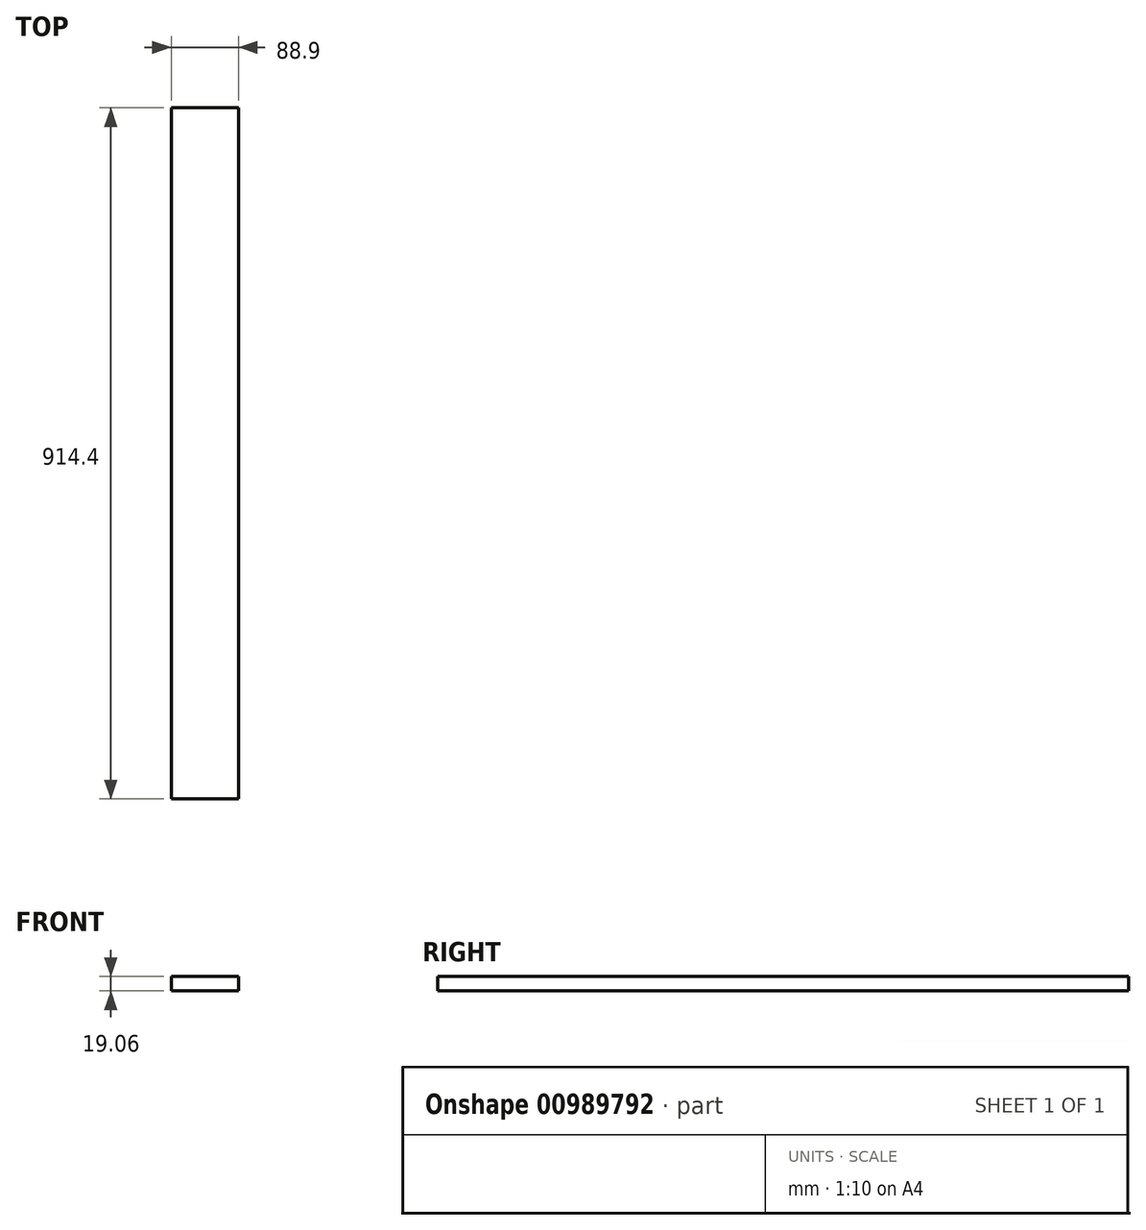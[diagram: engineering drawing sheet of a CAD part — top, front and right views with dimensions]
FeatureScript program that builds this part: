
annotation { "Feature Type Name" : "Feature", "Feature Type Description" : "" }
export const myFeature = defineFeature(function(context is Context, id is Id, definition is map)
    precondition{}
    {
        {
            var Q0;
            Q0=qCreatedBy(makeId("Front.planeOp"),FACE);
            var sketch = newSketch(context, id + "F0", { "sketchPlane" : qUnion([Q0])});
            skLineSegment(sketch, "E0.bottom", {"start": v(-44.45, 9.53) * mm, "end": v(44.45, 9.52) * mm});
            skLineSegment(sketch, "E0.top", {"start": v(-44.45, -9.52) * mm, "end": v(44.45, -9.53) * mm});
            skLineSegment(sketch, "E0.left", {"start": v(-44.45, 9.52) * mm, "end": v(-44.45, -9.52) * mm});
            skLineSegment(sketch, "E0.right", {"start": v(44.45, 9.52) * mm, "end": v(44.45, -9.52) * mm});
            skSolve(sketch);
        }
        {
            var Q0;
            Q0=makeQuery(id+"F0.imprint","IMPRINT",FACE,{"disambiguationData":[TD([[makeQuery(id+"F0.imprint","IMPRINT",EDGE,{"derivedFrom":sQuery(id+"F0.wireOp",EDGE,"E0.bottom")}),-1.0]])]});
            extrude(context, id + "F1", {"entities" : qUnion([Q0]), "endBound" : BoundingType.SYMMETRIC, "depth" : 914.4 * mm, "offsetDistance" : 25.4 * mm});
        }
    });
